# Revit family: Lithium Lifelight Recessed Emergency_Hosted_R18
name_source: partatom
category: Lighting Fixtures
revit_build: Autodesk Revit 2018 (Build: 20170223_1515(x64)
units: mm (PartAtom-declared; Revit-internal decimal feet)

## family parameters
Cut with Voids When Loaded = No
Host = Face
Light Source = Yes
Part Type = Normal
Room Calculation Point = No
Round Connector Dimension = Use Diameter
Shared = No

## types (1)
- LLIFE
    AS2293 = C0=D32, C90=D32
    Apparent Load = 3 W
    Battery = P/N: 1530010, L10 3.3V 2.5AH
    Ceiling Hole Cut-Out Radius = 43 mm
    Charging Method = Intelligent Current Limited Constant Voltage
    Color Filter = 16777215
    Colour = Plastic - Polycarbonate - White
    Default Elevation = 1219 mm
    Description = Lifelight, High Performance, Recessed emergency light
    Dimming Lamp Color Temperature Shift = <None>
    Height = 42 mm
    Inverter Board = LLIFE-CKIT,
    Lamp = 1100860, Lifelight Head Assembly,Round,1LED, L10
    Length = 232 mm
    Manufacturer = Clevertronics
    Model = ZLIFE
    Mounting = Recessed Ceiling
    Operating Mode = Non-Maintained
    Operating Voltage = 240 V
    Photometric Web File = Lifelight Recessed Emergency.ies
    Power Consumption = 3 W
    Testing System = Manual Test Switch
    Tilt Angle = -90.00°
    Width = 51 mm

## geometry (parser evidence)
native form markers: Blend x22, Sweep x3
no freeform markers — native parametric forms only
